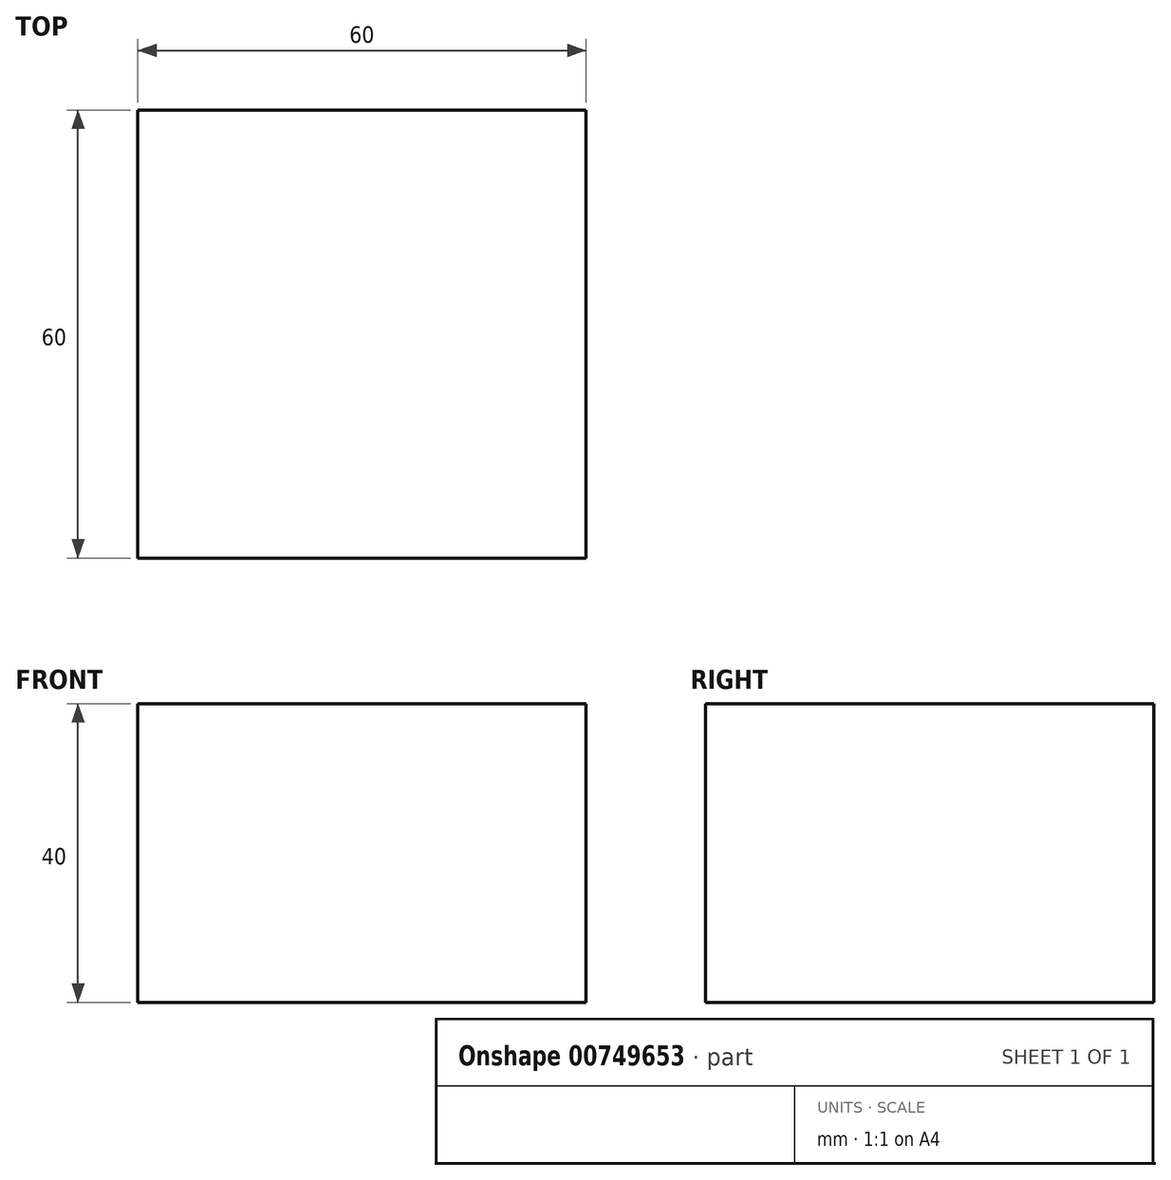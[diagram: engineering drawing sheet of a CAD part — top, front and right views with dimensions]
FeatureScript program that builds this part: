
annotation { "Feature Type Name" : "Feature", "Feature Type Description" : "" }
export const myFeature = defineFeature(function(context is Context, id is Id, definition is map)
    precondition{}
    {
        {
            var Q0;
            Q0=qCreatedBy(makeId("Top.planeOp"),FACE);
            var sketch = newSketch(context, id + "F0", { "sketchPlane" : qUnion([Q0])});
            skLineSegment(sketch, "E0.bottom", {"start": v(0, 0) * mm, "end": v(60, 0) * mm});
            skLineSegment(sketch, "E0.top", {"start": v(0, 60) * mm, "end": v(60, 60) * mm});
            skLineSegment(sketch, "E0.left", {"start": v(0, 0) * mm, "end": v(0, 60) * mm});
            skLineSegment(sketch, "E0.right", {"start": v(60, 0) * mm, "end": v(60, 60) * mm});
            skSolve(sketch);
        }
        {
            var Q0;
            Q0 = qSketchRegion(id + "F0", true);
            extrude(context, id + "F1", {"entities" : qUnion([Q0]), "depth" : 40 * mm, "offsetDistance" : 25 * mm});
        }
    });
